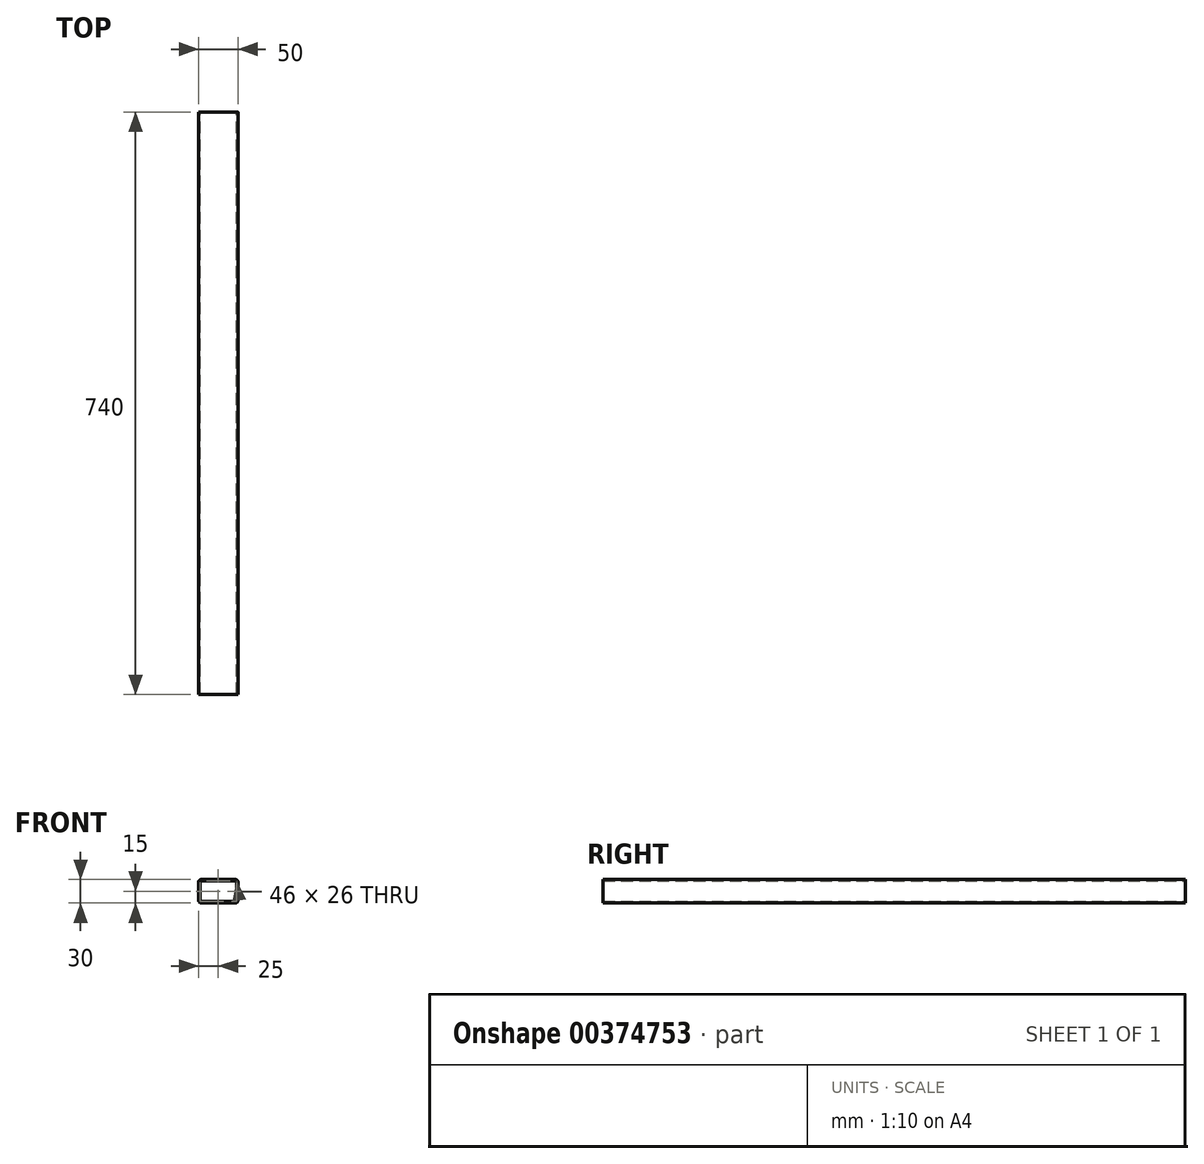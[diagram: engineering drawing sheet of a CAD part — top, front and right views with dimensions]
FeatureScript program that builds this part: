
annotation { "Feature Type Name" : "Feature", "Feature Type Description" : "" }
export const myFeature = defineFeature(function(context is Context, id is Id, definition is map)
    precondition{}
    {
        {
            var Q0;
            Q0=qCreatedBy(makeId("Front.planeOp"),FACE);
            var sketch = newSketch(context, id + "F0", { "sketchPlane" : qUnion([Q0])});
            skLineSegment(sketch, "E0.bottom", {"start": v(23, -13) * mm, "end": v(-23, -13) * mm});
            skLineSegment(sketch, "E0.top", {"start": v(23, 13) * mm, "end": v(-23, 13) * mm});
            skLineSegment(sketch, "E0.left", {"start": v(23, -13) * mm, "end": v(23, 13) * mm});
            skLineSegment(sketch, "E0.right", {"start": v(-23, -13) * mm, "end": v(-23, 13) * mm});
            skPoint(sketch, "E0.middle", {"position": v(0, 0) * mm});
            skLineSegment(sketch, "E1.bottom", {"start": v(21.5, -15) * mm, "end": v(-21.5, -15) * mm});
            skLineSegment(sketch, "E1.top", {"start": v(21.5, 15) * mm, "end": v(-21.5, 15) * mm});
            skLineSegment(sketch, "E1.left", {"start": v(25, -11.5) * mm, "end": v(25, 11.5) * mm});
            skLineSegment(sketch, "E1.right", {"start": v(-25, -11.5) * mm, "end": v(-25, 11.5) * mm});
            skPoint(sketch, "E2.visualSharp", {"position": v(-25, 15) * mm});
            skArc(sketch, "E2.filletArc", {"start": v(-21.5, 15) * mm, "mid": v(-23.97, 13.97) * mm, "end": v(-25, 11.5) * mm});
            skPoint(sketch, "E3.visualSharp", {"position": v(25, 15) * mm});
            skArc(sketch, "E3.filletArc", {"start": v(25, 11.5) * mm, "mid": v(23.97, 13.97) * mm, "end": v(21.5, 15) * mm});
            skPoint(sketch, "E4.visualSharp", {"position": v(25, -15) * mm});
            skArc(sketch, "E4.filletArc", {"start": v(21.5, -15) * mm, "mid": v(23.97, -13.97) * mm, "end": v(25, -11.5) * mm});
            skPoint(sketch, "E5.visualSharp", {"position": v(-25, -15) * mm});
            skArc(sketch, "E5.filletArc", {"start": v(-25, -11.5) * mm, "mid": v(-23.97, -13.97) * mm, "end": v(-21.5, -15) * mm});
            skSolve(sketch);
        }
        {
            var Q0;
            Q0=makeQuery(id+"F0.imprint","IMPRINT",FACE,{"disambiguationData":[TD([[makeQuery(id+"F0.imprint","IMPRINT",EDGE,{"derivedFrom":sQuery(id+"F0.wireOp",EDGE,"E0.bottom")}),1.0]])]});
            extrude(context, id + "F1", {"entities" : qUnion([Q0]), "depth" : 740 * mm, "offsetDistance" : 25 * mm});
        }
    });
